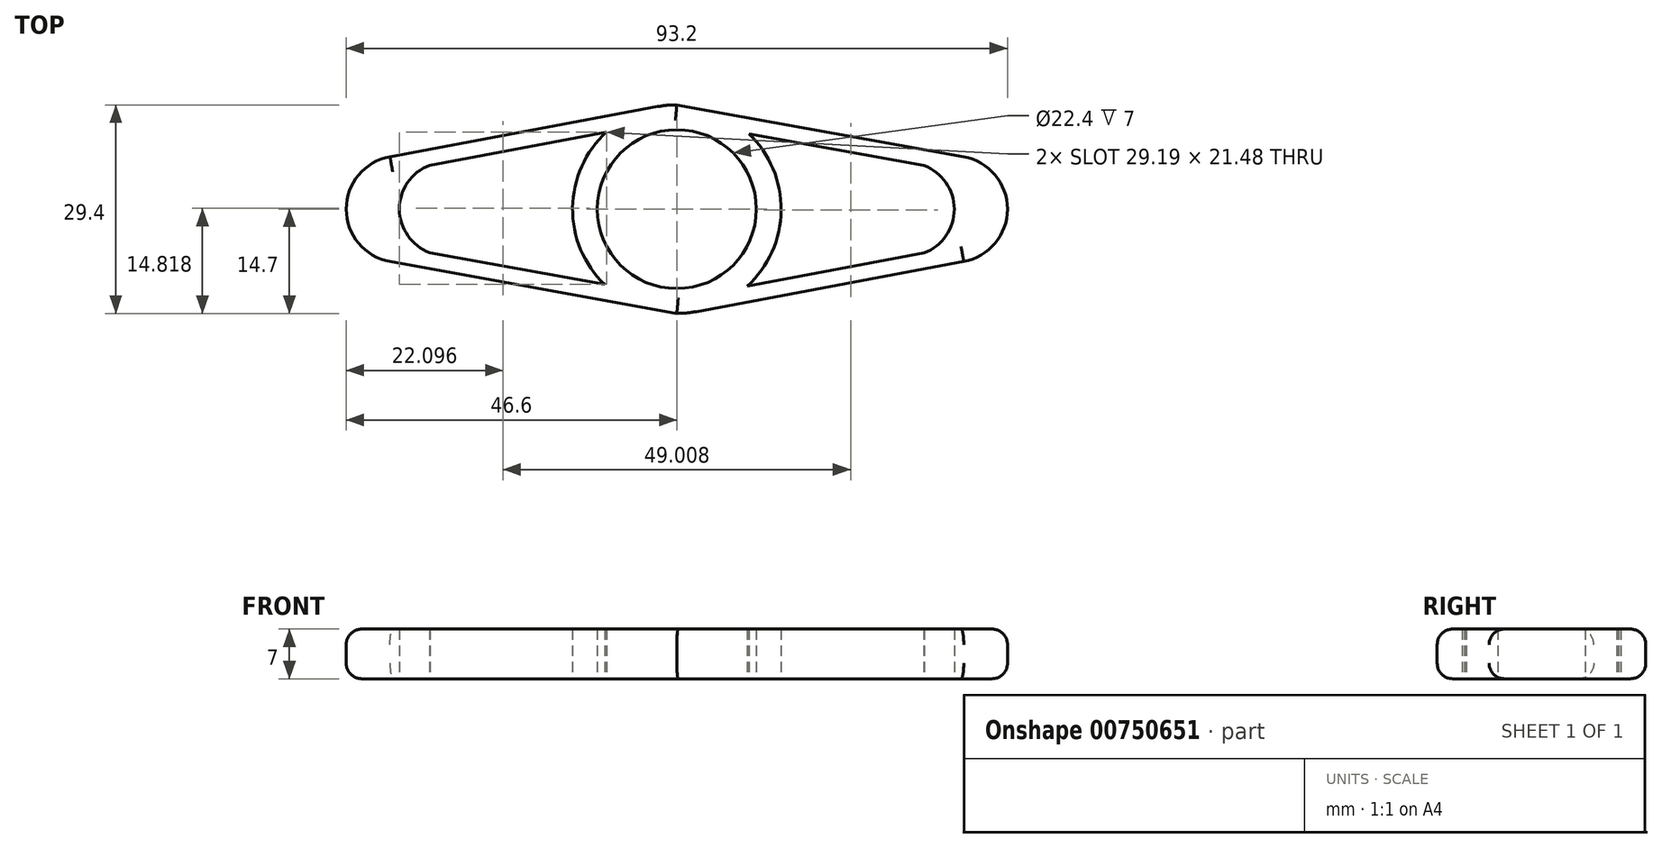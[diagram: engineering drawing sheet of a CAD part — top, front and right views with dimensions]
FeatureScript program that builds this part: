
annotation { "Feature Type Name" : "Feature", "Feature Type Description" : "" }
export const myFeature = defineFeature(function(context is Context, id is Id, definition is map)
    precondition{}
    {
        {
            var Q0;
            Q0=qCreatedBy(makeId("Top.planeOp"),FACE);
            var sketch = newSketch(context, id + "F0", { "sketchPlane" : qUnion([Q0])});
            skCircle(sketch, "E0", {"center": v(0, 0) * mm, "radius": 11.2 * mm});
            skCircle(sketch, "E1", {"center": v(0, 0) * mm, "radius": 14.7 * mm});
            skArc(sketch, "E2", {"start": v(34.85, -6.18) * mm, "mid": v(46.6, 0.02) * mm, "end": v(34.82, 6.16) * mm});
            skLineSegment(sketch, "E3", {"start": v(0, 14.7) * mm, "end": v(40.43, 7.38) * mm});
            skLineSegment(sketch, "E4", {"start": v(10.16, 10.62) * mm, "end": v(34.82, 6.16) * mm});
            skLineSegment(sketch, "E5", {"start": v(40.43, -7.38) * mm, "end": v(0, -14.96) * mm});
            skLineSegment(sketch, "E6", {"start": v(9.91, -10.86) * mm, "end": v(34.85, -6.18) * mm});
            skArc(sketch, "E7", {"start": v(34.85, -6.18) * mm, "mid": v(39.1, 0) * mm, "end": v(34.82, 6.16) * mm});
            skLineSegment(sketch, "E8.1.0", {"start": v(-9.91, 10.86) * mm, "end": v(-34.85, 6.18) * mm});
            skArc(sketch, "E8.1.1", {"start": v(-34.85, 6.18) * mm, "mid": v(-39.1, 0) * mm, "end": v(-34.82, -6.16) * mm});
            skLineSegment(sketch, "E8.1.2", {"start": v(-10.16, -10.62) * mm, "end": v(-34.82, -6.16) * mm});
            skArc(sketch, "E8.1.3", {"start": v(-34.85, 6.18) * mm, "mid": v(-46.6, -0.02) * mm, "end": v(-34.82, -6.16) * mm});
            skLineSegment(sketch, "E8.1.4", {"start": v(0, -14.7) * mm, "end": v(-40.43, -7.38) * mm});
            skLineSegment(sketch, "E8.1.5", {"start": v(-40.43, 7.38) * mm, "end": v(0, 14.96) * mm});
            skSolve(sketch);
        }
        {
            var Q0;
            {var subQ0=sQuery(id+"F0.wireOp",EDGE,"E8.1.1");Q0=makeQuery(id+"F0.imprint","IMPRINT",FACE,{"disambiguationData":[TD([[makeQuery(id+"F0.imprint","IMPRINT",EDGE,{"derivedFrom":subQ0}),-1.0]])]});}
            var Q1;
            {var subQ0=sQuery(id+"F0.wireOp",EDGE,"E8.1.2");Q1=makeQuery(id+"F0.imprint","IMPRINT",FACE,{"disambiguationData":[TD([[makeQuery(id+"F0.imprint","IMPRINT",EDGE,{"derivedFrom":subQ0}),1.0]])]});}
            var Q2;
            {var subQ0=sQuery(id+"F0.wireOp",EDGE,"E8.1.0");Q2=makeQuery(id+"F0.imprint","IMPRINT",FACE,{"disambiguationData":[TD([[makeQuery(id+"F0.imprint","IMPRINT",EDGE,{"derivedFrom":subQ0}),-1.0]])]});}
            var Q3;
            Q3=makeQuery(id+"F0.imprint","IMPRINT",FACE,{"disambiguationData":[TD([[makeQuery(id+"F0.imprint","IMPRINT",EDGE,{"derivedFrom":sQuery(id+"F0.wireOp",EDGE,"E0")}),-1.0]])]});
            var Q4;
            {var subQ0=sQuery(id+"F0.wireOp",EDGE,"E6");Q4=makeQuery(id+"F0.imprint","IMPRINT",FACE,{"disambiguationData":[TD([[makeQuery(id+"F0.imprint","IMPRINT",EDGE,{"derivedFrom":subQ0}),-1.0]])]});}
            var Q5;
            {var subQ0=sQuery(id+"F0.wireOp",EDGE,"E7");Q5=makeQuery(id+"F0.imprint","IMPRINT",FACE,{"disambiguationData":[TD([[makeQuery(id+"F0.imprint","IMPRINT",EDGE,{"derivedFrom":subQ0}),-1.0]])]});}
            var Q6;
            {var subQ0=sQuery(id+"F0.wireOp",EDGE,"E4");Q6=makeQuery(id+"F0.imprint","IMPRINT",FACE,{"disambiguationData":[TD([[makeQuery(id+"F0.imprint","IMPRINT",EDGE,{"derivedFrom":subQ0}),1.0]])]});}
            var Q7;
            Q7=sQuery(id+"F0.wireOp",EDGE,"E8.1.5");
            var Q8;
            Q8=sQuery(id+"F0.wireOp",EDGE,"E1");
            var Q9;
            Q9=sQuery(id+"F0.wireOp",EDGE,"E0");
            var Q10;
            Q10=sQuery(id+"F0.wireOp",EDGE,"E8.1.0");
            var Q11;
            Q11=sQuery(id+"F0.wireOp",EDGE,"E8.1.2");
            var Q12;
            Q12=sQuery(id+"F0.wireOp",EDGE,"E8.1.4");
            var Q13;
            Q13=sQuery(id+"F0.wireOp",EDGE,"E8.1.3");
            var Q14;
            Q14=sQuery(id+"F0.wireOp",EDGE,"E8.1.1");
            var Q15;
            Q15=sQuery(id+"F0.wireOp",EDGE,"E5");
            var Q16;
            Q16=sQuery(id+"F0.wireOp",EDGE,"E6");
            var Q17;
            Q17=sQuery(id+"F0.wireOp",EDGE,"E2");
            var Q18;
            Q18=sQuery(id+"F0.wireOp",EDGE,"E7");
            var Q19;
            Q19=sQuery(id+"F0.wireOp",EDGE,"E4");
            var Q20;
            Q20=sQuery(id+"F0.wireOp",EDGE,"E3");
            extrude(context, id + "F1", {"entities" : qUnion([Q0, Q1, Q2, Q3, Q4, Q5, Q6]), "surfaceEntities" : qUnion([Q7, Q8, Q9, Q10, Q11, Q12, Q13, Q14, Q15, Q16, Q17, Q18, Q19, Q20]), "depth" : 7 * mm, "offsetDistance" : 25 * mm});
        }
        {
            var Q0;
            Q0=makeQuery(id+"F1.opExtrude","CAP_EDGE",EDGE,{"disambiguationData":[OSD([sQuery(id+"F0.wireOp",EDGE,"E8.1.4")])],"isStart":false});
            var Q1;
            Q1=makeQuery(id+"F1.opExtrude","CAP_EDGE",EDGE,{"disambiguationData":[OSD([sQuery(id+"F0.wireOp",EDGE,"E8.1.3")])],"isStart":false});
            var Q2;
            Q2=makeQuery(id+"F1.opExtrude","CAP_EDGE",EDGE,{"disambiguationData":[OSD([sQuery(id+"F0.wireOp",EDGE,"E8.1.3")])],"isStart":true});
            var Q3;
            Q3=makeQuery(id+"F1.opExtrude","CAP_EDGE",EDGE,{"disambiguationData":[OSD([sQuery(id+"F0.wireOp",EDGE,"E8.1.4")])],"isStart":true});
            var Q4;
            Q4=makeQuery(id+"F1.opExtrude","CAP_EDGE",EDGE,{"disambiguationData":[OSD([sQuery(id+"F0.wireOp",EDGE,"E5")])],"isStart":false});
            var Q5;
            Q5=makeQuery(id+"F1.opExtrude","CAP_EDGE",EDGE,{"disambiguationData":[OSD([sQuery(id+"F0.wireOp",EDGE,"E5")])],"isStart":true});
            var Q6;
            {var subQ0=sQuery(id+"F0.wireOp",EDGE,"E1");Q6=makeQuery(id+"F1.opExtrude","CAP_EDGE",EDGE,{"disambiguationData":[OSD([subQ0]),TDD([makeQuery(id+"F0.imprint","IMPRINT",EDGE,{"disambiguationData":[TD([[makeQuery(id+"F0.imprint","INTERSECT",VERTEX,{"disambiguationData":[OD(0.0)],"derivedFrom":[subQ0,sQuery(id+"F0.wireOp",EDGE,"E8.1.4")]}),-1.0]])],"derivedFrom":subQ0})])],"isStart":true});}
            var Q7;
            {var subQ0=sQuery(id+"F0.wireOp",EDGE,"E1");Q7=makeQuery(id+"F1.opExtrude","CAP_EDGE",EDGE,{"disambiguationData":[OSD([subQ0]),TDD([makeQuery(id+"F0.imprint","IMPRINT",EDGE,{"disambiguationData":[TD([[makeQuery(id+"F0.imprint","INTERSECT",VERTEX,{"disambiguationData":[OD(0.0)],"derivedFrom":[subQ0,sQuery(id+"F0.wireOp",EDGE,"E8.1.4")]}),-1.0]])],"derivedFrom":subQ0})])],"isStart":false});}
            var Q8;
            {var subQ0=sQuery(id+"F0.wireOp",EDGE,"E1");Q8=makeQuery(id+"F1.opExtrude","CAP_EDGE",EDGE,{"disambiguationData":[OSD([subQ0]),TDD([makeQuery(id+"F0.imprint","IMPRINT",EDGE,{"disambiguationData":[TD([[makeQuery(id+"F0.imprint","INTERSECT",VERTEX,{"disambiguationData":[OD(0.0)],"derivedFrom":[subQ0,sQuery(id+"F0.wireOp",EDGE,"E3")]}),-1.0]])],"derivedFrom":subQ0})])],"isStart":false});}
            var Q9;
            Q9=makeQuery(id+"F1.opExtrude","CAP_EDGE",EDGE,{"disambiguationData":[OSD([sQuery(id+"F0.wireOp",EDGE,"E3")])],"isStart":false});
            var Q10;
            Q10=makeQuery(id+"F1.opExtrude","CAP_EDGE",EDGE,{"disambiguationData":[OSD([sQuery(id+"F0.wireOp",EDGE,"E2")])],"isStart":false});
            var Q11;
            Q11=makeQuery(id+"F1.opExtrude","CAP_EDGE",EDGE,{"disambiguationData":[OSD([sQuery(id+"F0.wireOp",EDGE,"E2")])],"isStart":true});
            var Q12;
            Q12=makeQuery(id+"F1.opExtrude","CAP_EDGE",EDGE,{"disambiguationData":[OSD([sQuery(id+"F0.wireOp",EDGE,"E3")])],"isStart":true});
            var Q13;
            {var subQ0=sQuery(id+"F0.wireOp",EDGE,"E1");Q13=makeQuery(id+"F1.opExtrude","CAP_EDGE",EDGE,{"disambiguationData":[OSD([subQ0]),TDD([makeQuery(id+"F0.imprint","IMPRINT",EDGE,{"disambiguationData":[TD([[makeQuery(id+"F0.imprint","INTERSECT",VERTEX,{"disambiguationData":[OD(0.0)],"derivedFrom":[subQ0,sQuery(id+"F0.wireOp",EDGE,"E3")]}),-1.0]])],"derivedFrom":subQ0})])],"isStart":true});}
            var Q14;
            Q14=makeQuery(id+"F1.opExtrude","CAP_EDGE",EDGE,{"disambiguationData":[OSD([sQuery(id+"F0.wireOp",EDGE,"E8.1.5")])],"isStart":false});
            fillet(context, id + "F2", {"entities" : qUnion([Q0, Q1, Q2, Q3, Q4, Q5, Q6, Q7, Q8, Q9, Q10, Q11, Q12, Q13, Q14]), "radius" : 2.17 * mm, "tangentPropagation" : true, "allowEdgeOverflow" : false});
        }
    });
